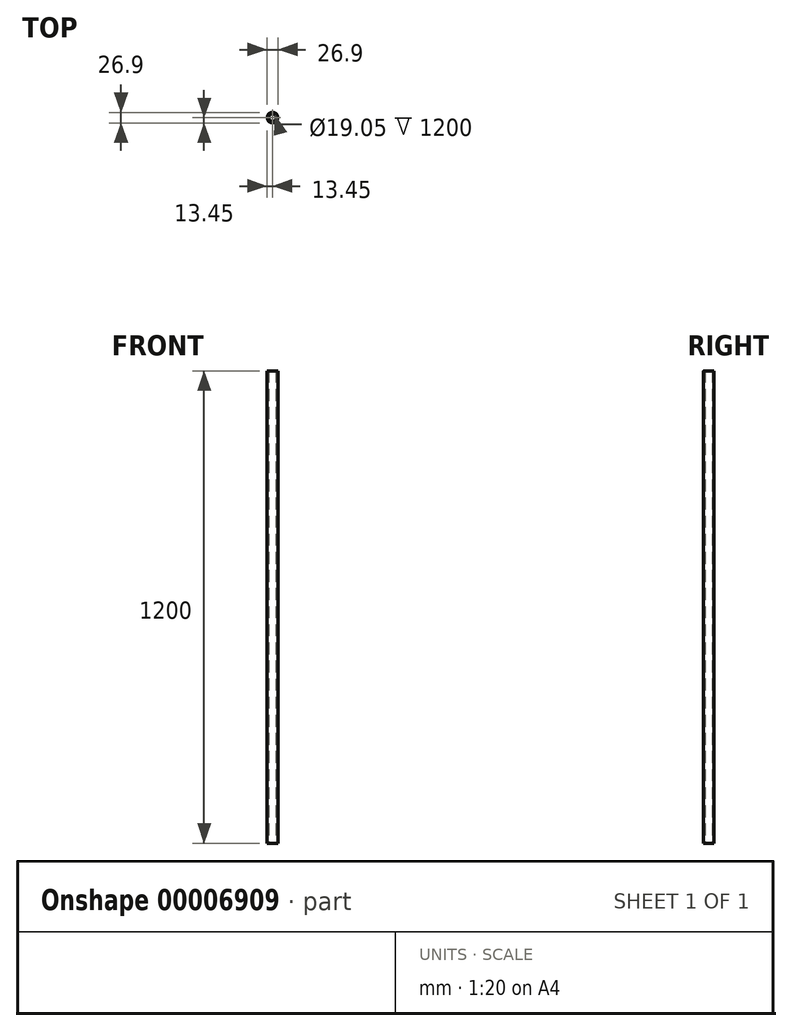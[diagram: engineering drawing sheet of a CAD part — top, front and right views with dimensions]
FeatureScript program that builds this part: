
annotation { "Feature Type Name" : "Feature", "Feature Type Description" : "" }
export const myFeature = defineFeature(function(context is Context, id is Id, definition is map)
    precondition{}
    {
        {
            var Q0;
            Q0=qCreatedBy(makeId("Top.planeOp"),FACE);
            var sketch = newSketch(context, id + "F0", { "sketchPlane" : qUnion([Q0])});
            skCircle(sketch, "E0", {"center": v(0, 0) * mm, "radius": 13.45 * mm});
            skCircle(sketch, "E1", {"center": v(0, 0) * mm, "radius": 9.53 * mm});
            skSolve(sketch);
        }
        {
            var Q0;
            Q0=makeQuery(id+"F0.imprint","IMPRINT",FACE,{"disambiguationData":[TD([[makeQuery(id+"F0.imprint","IMPRINT",EDGE,{"derivedFrom":sQuery(id+"F0.wireOp",EDGE,"E0")}),1.0]])]});
            extrude(context, id + "F1", {"entities" : qUnion([Q0]), "depth" : (1200) * mm});
        }
    });
